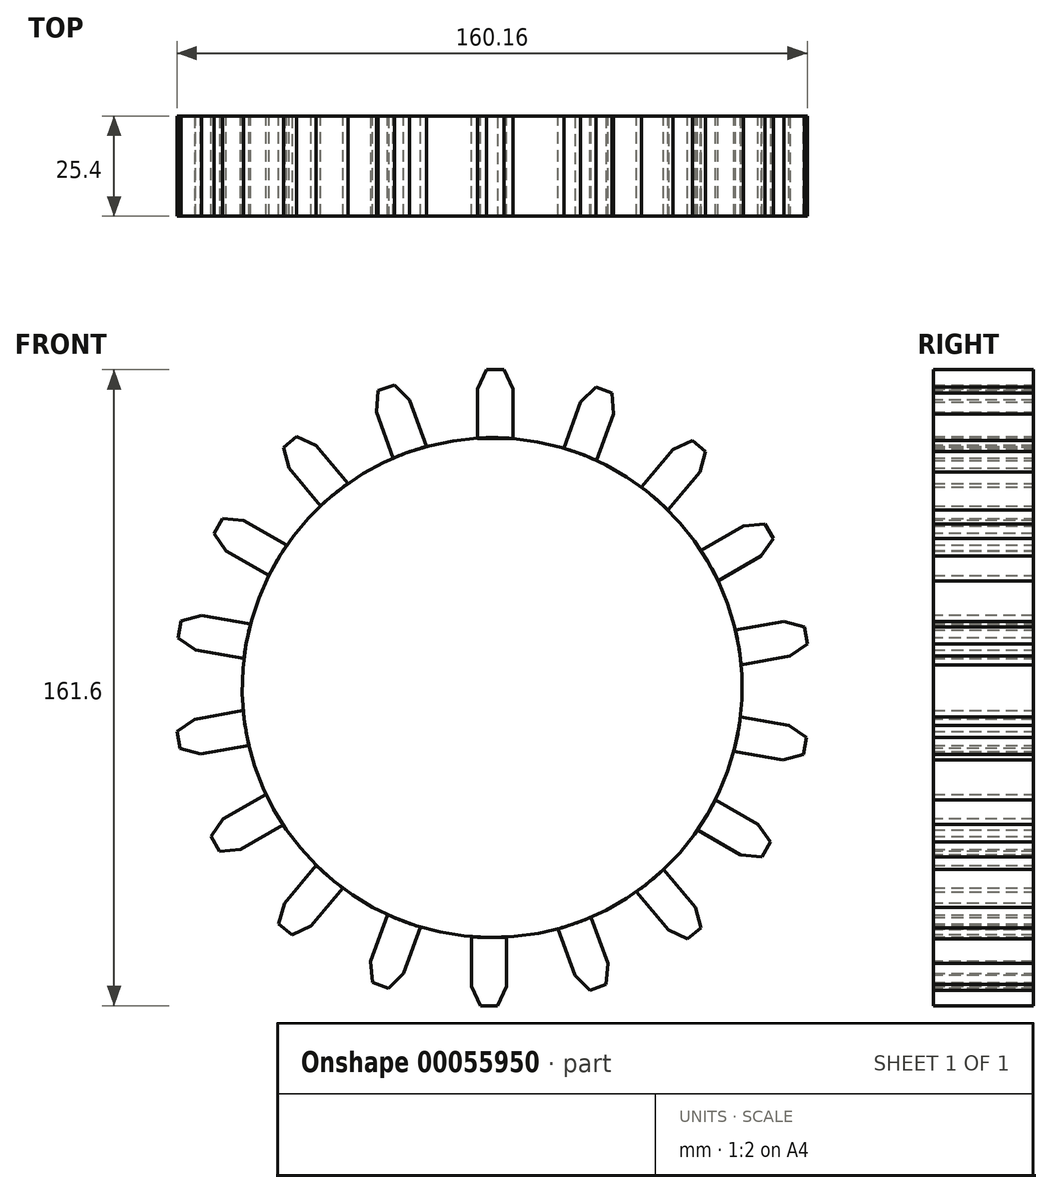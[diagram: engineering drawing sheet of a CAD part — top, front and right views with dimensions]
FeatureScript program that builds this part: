
annotation { "Feature Type Name" : "Feature", "Feature Type Description" : "" }
export const myFeature = defineFeature(function(context is Context, id is Id, definition is map)
    precondition{}
    {
        {
            var Q0;
            Q0=qCreatedBy(makeId("Front.planeOp"),FACE);
            var sketch = newSketch(context, id + "F0", { "sketchPlane" : qUnion([Q0])});
            skCircle(sketch, "E0", {"center": v(0, 0) * mm, "radius": 63.5 * mm});
            skLineSegment(sketch, "E1.bottom", {"start": v(-3.68, 80.8) * mm, "end": v(5.24, 80.8) * mm});
            skLineSegment(sketch, "E1.top", {"start": v(-3.68, 63.28) * mm, "end": v(5.24, 63.28) * mm});
            skLineSegment(sketch, "E1.left", {"start": v(-3.68, 80.8) * mm, "end": v(-3.68, 63.28) * mm});
            skLineSegment(sketch, "E1.right", {"start": v(5.24, 80.8) * mm, "end": v(5.24, 63.28) * mm});
            skSolve(sketch);
        }
        {
            var Q0;
            {var subQ0=sQuery(id+"F0.wireOp",EDGE,"E1.top");Q0=makeQuery(id+"F0.imprint","IMPRINT",FACE,{"disambiguationData":[TD([[makeQuery(id+"F0.imprint","IMPRINT",EDGE,{"derivedFrom":subQ0}),-1.0]])]});}
            var Q1;
            {var subQ4=sQuery(id+"F0.wireOp",EDGE,"E1.bottom");Q1=makeQuery(id+"F0.imprint","IMPRINT",FACE,{"disambiguationData":[TD([[makeQuery(id+"F0.imprint","IMPRINT",EDGE,{"derivedFrom":subQ4}),-1.0]])]});}
            extrude(context, id + "F1", {"entities" : qUnion([Q0, Q1]), "depth" : 25.4 * mm});
        }
        {
            var Q0;
            Q0=makeQuery(id+"F1.opExtrude","SWEPT_EDGE",EDGE,{"disambiguationData":[OSD([sQuery(id+"F0.wireOp",EDGE,"E1.bottom"),sQuery(id+"F0.wireOp",EDGE,"E1.right")])]});
            var Q1;
            Q1=makeQuery(id+"F1.opExtrude","SWEPT_EDGE",EDGE,{"disambiguationData":[OSD([sQuery(id+"F0.wireOp",EDGE,"E1.bottom"),sQuery(id+"F0.wireOp",EDGE,"E1.left")])]});
            chamfer(context, id + "F2", {"entities" : qUnion([Q0, Q1]), "chamferType" : ChamferType.OFFSET_ANGLE, "width" : 2.3 * mm, "oppositeDirection" : false, "angle" : 65 * degree, "tangentPropagation" : true});
        }
        {
            var Q0;
            Q0=makeQuery(id+"F1.opExtrude","SWEPT_BODY",BODY,{"disambiguationData":[OSD([sQuery(id+"F0.wireOp",EDGE,"E0"),sQuery(id+"F0.wireOp",EDGE,"E1.bottom"),sQuery(id+"F0.wireOp",EDGE,"E1.left"),sQuery(id+"F0.wireOp",EDGE,"E1.right")])]});
            var Q1;
            {var subQ0=sQuery(id+"F0.wireOp",EDGE,"E0");Q1=makeQuery(id+"F1.opExtrude","SWEPT_FACE",FACE,{"disambiguationData":[OSD([subQ0]),TDD([makeQuery(id+"F0.imprint","IMPRINT",EDGE,{"disambiguationData":[TD([[makeQuery(id+"F0.imprint","INTERSECT",VERTEX,{"derivedFrom":[subQ0,sQuery(id+"F0.wireOp",EDGE,"E1.left")]}),-1.0]])],"derivedFrom":subQ0})])]});}
            circularPattern(context, id + "F3", {"entities" : qUnion([Q0]), "axis" : qUnion([Q1]), "angle" : 20 * degree, "instanceCount" : 20});
        }
    });
